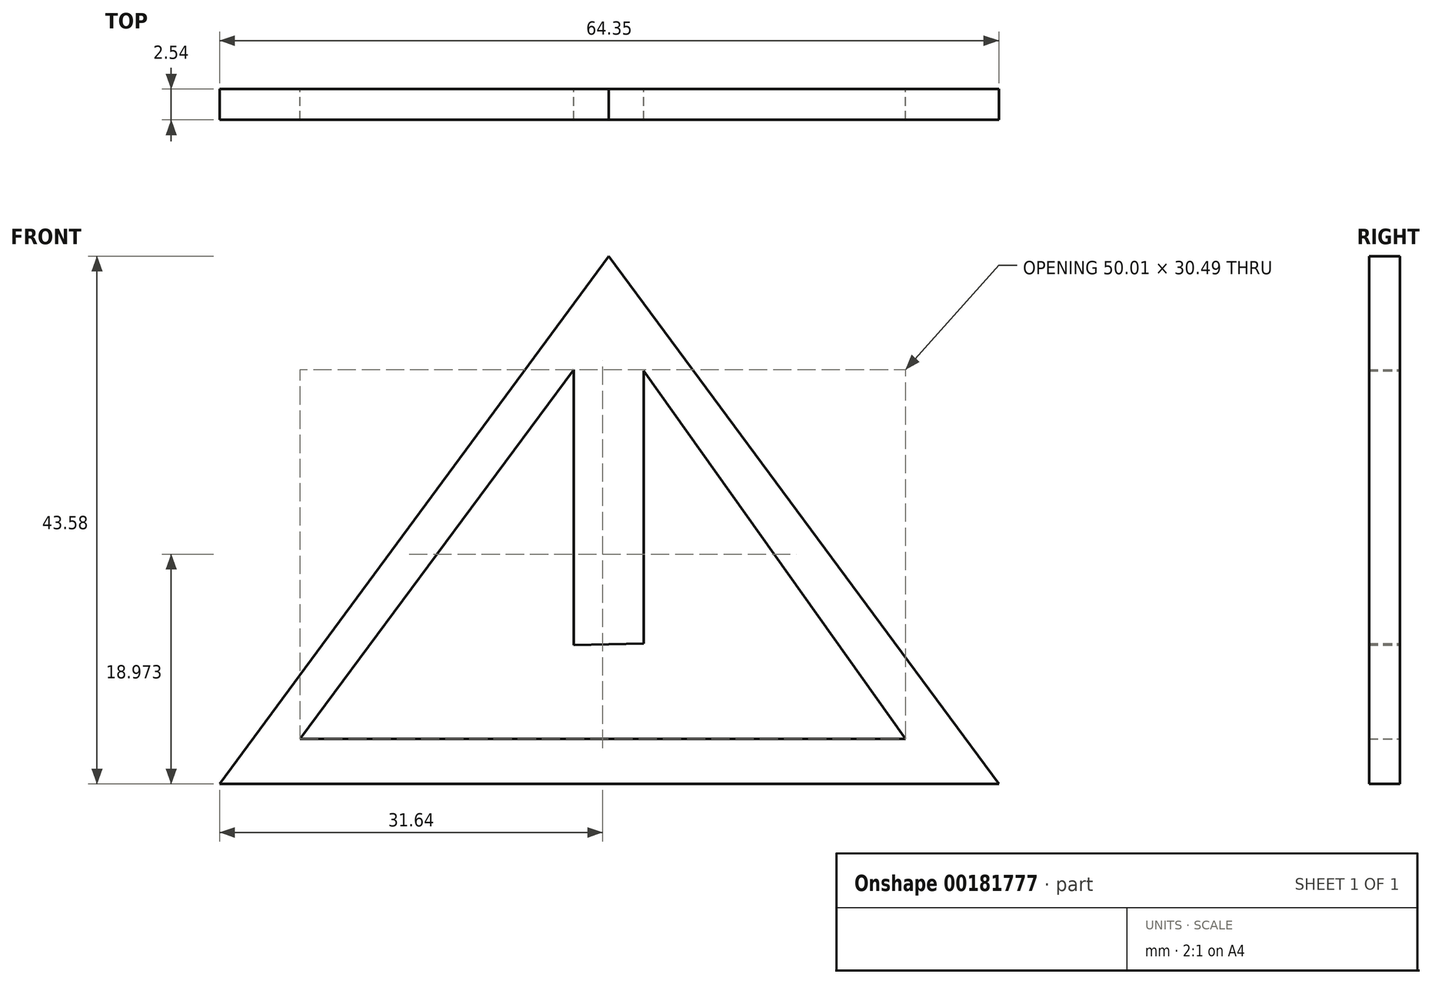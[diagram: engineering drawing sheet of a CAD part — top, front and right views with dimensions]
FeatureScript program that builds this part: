
annotation { "Feature Type Name" : "Feature", "Feature Type Description" : "" }
export const myFeature = defineFeature(function(context is Context, id is Id, definition is map)
    precondition{}
    {
        {
            var Q0;
            Q0=qCreatedBy(makeId("Front.planeOp"),FACE);
            var sketch = newSketch(context, id + "F0", { "sketchPlane" : qUnion([Q0])});
            skLineSegment(sketch, "E0", {"start": v(0, 0) * mm, "end": v(32.2, 0) * mm});
            skLineSegment(sketch, "E1", {"start": v(0, 0) * mm, "end": v(-32.15, 0) * mm});
            skLineSegment(sketch, "E2", {"start": v(0, 43.58) * mm, "end": v(32.2, 0) * mm});
            skLineSegment(sketch, "E3", {"start": v(0, 43.58) * mm, "end": v(-32.15, 0) * mm});
            skLineSegment(sketch, "E4", {"start": v(-25.51, 3.73) * mm, "end": v(24.5, 3.73) * mm});
            skLineSegment(sketch, "E5", {"start": v(-2.91, 34.22) * mm, "end": v(-2.91, 11.47) * mm});
            skLineSegment(sketch, "E6", {"start": v(2.87, 34.12) * mm, "end": v(2.87, 11.6) * mm});
            skLineSegment(sketch, "E7", {"start": v(-2.91, 11.47) * mm, "end": v(2.87, 11.6) * mm});
            skLineSegment(sketch, "E8", {"start": v(-2.91, 34.22) * mm, "end": v(-25.51, 3.73) * mm});
            skLineSegment(sketch, "E9", {"start": v(2.87, 34.12) * mm, "end": v(24.5, 3.73) * mm});
            skSolve(sketch);
        }
        {
            var Q0;
            Q0=makeQuery(id+"F0.imprint","IMPRINT",FACE,{"disambiguationData":[TD([[makeQuery(id+"F0.imprint","IMPRINT",EDGE,{"derivedFrom":sQuery(id+"F0.wireOp",EDGE,"E0")}),1.0]])]});
            extrude(context, id + "F1", {"entities" : qUnion([Q0]), "endBound" : BoundingType.SYMMETRIC, "depth" : 2.54 * mm});
        }
    });
